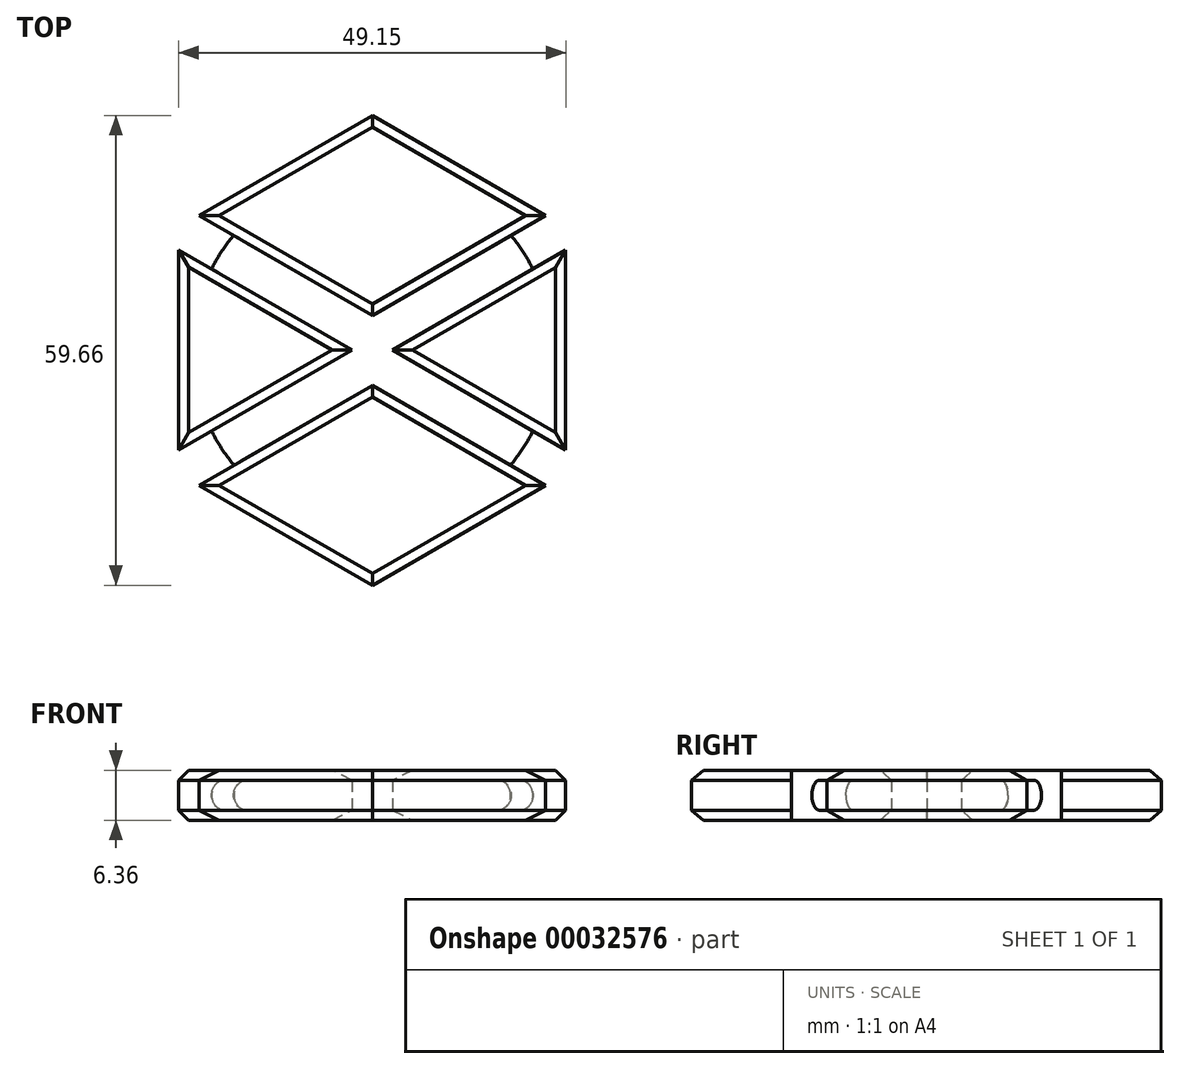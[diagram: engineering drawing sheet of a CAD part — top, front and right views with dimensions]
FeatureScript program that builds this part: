
annotation { "Feature Type Name" : "Feature", "Feature Type Description" : "" }
export const myFeature = defineFeature(function(context is Context, id is Id, definition is map)
    precondition{}
    {
        {
            var Q0;
            Q0=qCreatedBy(makeId("Top.planeOp"),FACE);
            var sketch = newSketch(context, id + "F0", { "sketchPlane" : qUnion([Q0])});
            skLineSegment(sketch, "E0", {"start": v(0, 0) * mm, "end": v(-22, 12.7) * mm});
            skLineSegment(sketch, "E1", {"start": v(-22, 12.7) * mm, "end": v(0, 25.4) * mm});
            skLineSegment(sketch, "E2", {"start": v(0, 25.4) * mm, "end": v(22, 12.7) * mm});
            skLineSegment(sketch, "E3", {"start": v(22, 12.7) * mm, "end": v(0, 0) * mm});
            skLineSegment(sketch, "E4", {"start": v(-2.6, 29.9) * mm, "end": v(-24.6, 17.2) * mm});
            skLineSegment(sketch, "E5", {"start": v(-24.6, 17.2) * mm, "end": v(-24.6, 42.6) * mm});
            skLineSegment(sketch, "E6", {"start": v(-24.6, 42.6) * mm, "end": v(-2.6, 29.9) * mm});
            skLineSegment(sketch, "E7", {"start": v(0, 34.26) * mm, "end": v(-22, 46.96) * mm});
            skLineSegment(sketch, "E8", {"start": v(-22, 46.96) * mm, "end": v(0, 59.66) * mm});
            skLineSegment(sketch, "E9", {"start": v(0, 59.66) * mm, "end": v(22, 46.96) * mm});
            skLineSegment(sketch, "E10", {"start": v(22, 46.96) * mm, "end": v(0, 34.26) * mm});
            skLineSegment(sketch, "E11", {"start": v(2.56, 29.87) * mm, "end": v(24.56, 17.17) * mm});
            skLineSegment(sketch, "E12", {"start": v(24.56, 17.17) * mm, "end": v(24.56, 42.57) * mm});
            skLineSegment(sketch, "E13", {"start": v(24.56, 42.57) * mm, "end": v(2.56, 29.87) * mm});
            skLineSegment(sketch, "E14", {"start": v(0, 25.4) * mm, "end": v(-2.6, 29.9) * mm});
            skLineSegment(sketch, "E15", {"start": v(-2.6, 29.9) * mm, "end": v(0, 34.26) * mm});
            skLineSegment(sketch, "E16", {"start": v(0, 34.26) * mm, "end": v(2.56, 29.87) * mm});
            skLineSegment(sketch, "E17", {"start": v(2.56, 29.87) * mm, "end": v(0, 25.4) * mm});
            skCircle(sketch, "E18", {"center": v(-0.02, 29.89) * mm, "radius": 22.86 * mm});
            skPoint(sketch, "E19", {"position": v(0, 46.96) * mm});
            skSolve(sketch);
        }
        {
            var Q0;
            {var subQ6=sQuery(id+"F0.wireOp",EDGE,"E8");Q0=makeQuery(id+"F0.imprint","IMPRINT",FACE,{"disambiguationData":[TD([[makeQuery(id+"F0.imprint","IMPRINT",EDGE,{"derivedFrom":subQ6}),-1.0]])]});}
            var Q1;
            {var subQ1=sQuery(id+"F0.wireOp",EDGE,"E18");var subQ3=sQuery(id+"F0.wireOp",EDGE,"E7");var subQ5=makeQuery(id+"F0.imprint","INTERSECT",VERTEX,{"derivedFrom":[subQ3,subQ1]});Q1=makeQuery(id+"F0.imprint","IMPRINT",FACE,{"disambiguationData":[TD([[makeQuery(id+"F0.imprint","IMPRINT",EDGE,{"disambiguationData":[TD([[subQ5,1.0]])],"derivedFrom":subQ1}),1.0]])]});}
            var Q2;
            {var subQ0=sQuery(id+"F0.wireOp",EDGE,"E18");var subQ3=sQuery(id+"F0.wireOp",EDGE,"E11");var subQ4=makeQuery(id+"F0.imprint","INTERSECT",VERTEX,{"derivedFrom":[subQ3,subQ0]});Q2=makeQuery(id+"F0.imprint","IMPRINT",FACE,{"disambiguationData":[TD([[makeQuery(id+"F0.imprint","IMPRINT",EDGE,{"disambiguationData":[TD([[subQ4,-1.0]])],"derivedFrom":subQ0}),1.0]])]});}
            var Q3;
            {var subQ5=sQuery(id+"F0.wireOp",EDGE,"E12");Q3=makeQuery(id+"F0.imprint","IMPRINT",FACE,{"disambiguationData":[TD([[makeQuery(id+"F0.imprint","IMPRINT",EDGE,{"derivedFrom":subQ5}),1.0]])]});}
            var Q4;
            {var subQ6=sQuery(id+"F0.wireOp",EDGE,"E0");Q4=makeQuery(id+"F0.imprint","IMPRINT",FACE,{"disambiguationData":[TD([[makeQuery(id+"F0.imprint","IMPRINT",EDGE,{"derivedFrom":subQ6}),-1.0]])]});}
            var Q5;
            {var subQ0=sQuery(id+"F0.wireOp",EDGE,"E18");var subQ3=sQuery(id+"F0.wireOp",EDGE,"E1");var subQ4=makeQuery(id+"F0.imprint","INTERSECT",VERTEX,{"derivedFrom":[subQ3,subQ0]});Q5=makeQuery(id+"F0.imprint","IMPRINT",FACE,{"disambiguationData":[TD([[makeQuery(id+"F0.imprint","IMPRINT",EDGE,{"disambiguationData":[TD([[subQ4,-1.0]])],"derivedFrom":subQ0}),1.0]])]});}
            var Q6;
            {var subQ5=sQuery(id+"F0.wireOp",EDGE,"E5");Q6=makeQuery(id+"F0.imprint","IMPRINT",FACE,{"disambiguationData":[TD([[makeQuery(id+"F0.imprint","IMPRINT",EDGE,{"derivedFrom":subQ5}),-1.0]])]});}
            var Q7;
            {var subQ0=sQuery(id+"F0.wireOp",EDGE,"E18");var subQ3=sQuery(id+"F0.wireOp",EDGE,"E4");var subQ4=makeQuery(id+"F0.imprint","INTERSECT",VERTEX,{"derivedFrom":[subQ3,subQ0]});Q7=makeQuery(id+"F0.imprint","IMPRINT",FACE,{"disambiguationData":[TD([[makeQuery(id+"F0.imprint","IMPRINT",EDGE,{"disambiguationData":[TD([[subQ4,1.0]])],"derivedFrom":subQ0}),1.0]])]});}
            extrude(context, id + "F1", {"entities" : qUnion([Q0, Q1, Q2, Q3, Q4, Q5, Q6, Q7]), "endBound" : BoundingType.SYMMETRIC, "depth" : 6.35 * mm});
        }
        {
            var Q0;
            {var subQ5=sQuery(id+"F0.wireOp",EDGE,"E16");Q0=makeQuery(id+"F0.imprint","IMPRINT",FACE,{"disambiguationData":[TD([[makeQuery(id+"F0.imprint","IMPRINT",EDGE,{"derivedFrom":subQ5}),1.0]])]});}
            var Q1;
            Q1=makeQuery(id+"F0.imprint","IMPRINT",FACE,{"disambiguationData":[TD([[makeQuery(id+"F0.imprint","IMPRINT",EDGE,{"derivedFrom":sQuery(id+"F0.wireOp",EDGE,"E14")}),-1.0]])]});
            var Q2;
            {var subQ5=sQuery(id+"F0.wireOp",EDGE,"E15");Q2=makeQuery(id+"F0.imprint","IMPRINT",FACE,{"disambiguationData":[TD([[makeQuery(id+"F0.imprint","IMPRINT",EDGE,{"derivedFrom":subQ5}),1.0]])]});}
            var Q3;
            {var subQ5=sQuery(id+"F0.wireOp",EDGE,"E14");Q3=makeQuery(id+"F0.imprint","IMPRINT",FACE,{"disambiguationData":[TD([[makeQuery(id+"F0.imprint","IMPRINT",EDGE,{"derivedFrom":subQ5}),1.0]])]});}
            var Q4;
            {var subQ5=sQuery(id+"F0.wireOp",EDGE,"E17");Q4=makeQuery(id+"F0.imprint","IMPRINT",FACE,{"disambiguationData":[TD([[makeQuery(id+"F0.imprint","IMPRINT",EDGE,{"derivedFrom":subQ5}),1.0]])]});}
            extrude(context, id + "F2", {"entities" : qUnion([Q0, Q1, Q2, Q3, Q4]), "endBound" : BoundingType.SYMMETRIC, "depth" : 3.8 * mm});
        }
        {
            var Q0;
            {var subQ0=sQuery(id+"F0.wireOp",EDGE,"E18");Q0=makeQuery(id+"F2.opExtrude","CAP_EDGE",EDGE,{"disambiguationData":[OSD([subQ0]),TDD([makeQuery(id+"F0.imprint","IMPRINT",EDGE,{"disambiguationData":[TD([[makeQuery(id+"F0.imprint","INTERSECT",VERTEX,{"derivedFrom":[sQuery(id+"F0.wireOp",EDGE,"E6"),subQ0]}),1.0]])],"derivedFrom":subQ0})])],"isStart":false});}
            var Q1;
            {var subQ0=sQuery(id+"F0.wireOp",EDGE,"E18");Q1=makeQuery(id+"F2.opExtrude","CAP_EDGE",EDGE,{"disambiguationData":[OSD([subQ0]),TDD([makeQuery(id+"F0.imprint","IMPRINT",EDGE,{"disambiguationData":[TD([[makeQuery(id+"F0.imprint","INTERSECT",VERTEX,{"derivedFrom":[sQuery(id+"F0.wireOp",EDGE,"E6"),subQ0]}),1.0]])],"derivedFrom":subQ0})])],"isStart":true});}
            var Q2;
            {var subQ0=sQuery(id+"F0.wireOp",EDGE,"E18");Q2=makeQuery(id+"F2.opExtrude","CAP_EDGE",EDGE,{"disambiguationData":[OSD([subQ0]),TDD([makeQuery(id+"F0.imprint","IMPRINT",EDGE,{"disambiguationData":[TD([[makeQuery(id+"F0.imprint","INTERSECT",VERTEX,{"derivedFrom":[sQuery(id+"F0.wireOp",EDGE,"E1"),subQ0]}),1.0]])],"derivedFrom":subQ0})])],"isStart":false});}
            var Q3;
            {var subQ0=sQuery(id+"F0.wireOp",EDGE,"E18");Q3=makeQuery(id+"F2.opExtrude","CAP_EDGE",EDGE,{"disambiguationData":[OSD([subQ0]),TDD([makeQuery(id+"F0.imprint","IMPRINT",EDGE,{"disambiguationData":[TD([[makeQuery(id+"F0.imprint","INTERSECT",VERTEX,{"derivedFrom":[sQuery(id+"F0.wireOp",EDGE,"E1"),subQ0]}),1.0]])],"derivedFrom":subQ0})])],"isStart":true});}
            var Q4;
            {var subQ0=sQuery(id+"F0.wireOp",EDGE,"E18");Q4=makeQuery(id+"F2.opExtrude","CAP_EDGE",EDGE,{"disambiguationData":[OSD([subQ0]),TDD([makeQuery(id+"F0.imprint","IMPRINT",EDGE,{"disambiguationData":[TD([[makeQuery(id+"F0.imprint","INTERSECT",VERTEX,{"derivedFrom":[sQuery(id+"F0.wireOp",EDGE,"E2"),subQ0]}),-1.0]])],"derivedFrom":subQ0})])],"isStart":true});}
            var Q5;
            {var subQ0=sQuery(id+"F0.wireOp",EDGE,"E18");Q5=makeQuery(id+"F2.opExtrude","CAP_EDGE",EDGE,{"disambiguationData":[OSD([subQ0]),TDD([makeQuery(id+"F0.imprint","IMPRINT",EDGE,{"disambiguationData":[TD([[makeQuery(id+"F0.imprint","INTERSECT",VERTEX,{"derivedFrom":[sQuery(id+"F0.wireOp",EDGE,"E2"),subQ0]}),-1.0]])],"derivedFrom":subQ0})])],"isStart":false});}
            var Q6;
            {var subQ0=sQuery(id+"F0.wireOp",EDGE,"E18");Q6=makeQuery(id+"F2.opExtrude","CAP_EDGE",EDGE,{"disambiguationData":[OSD([subQ0]),TDD([makeQuery(id+"F0.imprint","IMPRINT",EDGE,{"disambiguationData":[TD([[makeQuery(id+"F0.imprint","INTERSECT",VERTEX,{"derivedFrom":[sQuery(id+"F0.wireOp",EDGE,"E10"),subQ0]}),1.0]])],"derivedFrom":subQ0})])],"isStart":true});}
            var Q7;
            {var subQ0=sQuery(id+"F0.wireOp",EDGE,"E18");Q7=makeQuery(id+"F2.opExtrude","CAP_EDGE",EDGE,{"disambiguationData":[OSD([subQ0]),TDD([makeQuery(id+"F0.imprint","IMPRINT",EDGE,{"disambiguationData":[TD([[makeQuery(id+"F0.imprint","INTERSECT",VERTEX,{"derivedFrom":[sQuery(id+"F0.wireOp",EDGE,"E10"),subQ0]}),1.0]])],"derivedFrom":subQ0})])],"isStart":false});}
            fillet(context, id + "F3", {"entities" : qUnion([Q0, Q1, Q2, Q3, Q4, Q5, Q6, Q7]), "radius" : 1.9 * mm, "tangentPropagation" : true, "allowEdgeOverflow" : false});
        }
        {
            var Q0;
            Q0=makeQuery(id+"F1.opExtrude","CAP_EDGE",EDGE,{"disambiguationData":[OSD([sQuery(id+"F0.wireOp",EDGE,"E8")])],"isStart":false});
            var Q1;
            Q1=makeQuery(id+"F1.opExtrude","CAP_EDGE",EDGE,{"disambiguationData":[OSD([sQuery(id+"F0.wireOp",EDGE,"E8")])],"isStart":true});
            var Q2;
            Q2=makeQuery(id+"F1.opExtrude","CAP_EDGE",EDGE,{"disambiguationData":[OSD([sQuery(id+"F0.wireOp",EDGE,"E9")])],"isStart":true});
            var Q3;
            Q3=makeQuery(id+"F1.opExtrude","CAP_EDGE",EDGE,{"disambiguationData":[OSD([sQuery(id+"F0.wireOp",EDGE,"E9")])],"isStart":false});
            var Q4;
            Q4=makeQuery(id+"F1.opExtrude","CAP_EDGE",EDGE,{"disambiguationData":[OSD([sQuery(id+"F0.wireOp",EDGE,"E12")])],"isStart":false});
            var Q5;
            Q5=makeQuery(id+"F1.opExtrude","CAP_EDGE",EDGE,{"disambiguationData":[OSD([sQuery(id+"F0.wireOp",EDGE,"E12")])],"isStart":true});
            var Q6;
            Q6=makeQuery(id+"F1.opExtrude","CAP_EDGE",EDGE,{"disambiguationData":[OSD([sQuery(id+"F0.wireOp",EDGE,"E0")])],"isStart":true});
            var Q7;
            Q7=makeQuery(id+"F1.opExtrude","CAP_EDGE",EDGE,{"disambiguationData":[OSD([sQuery(id+"F0.wireOp",EDGE,"E0")])],"isStart":false});
            var Q8;
            Q8=makeQuery(id+"F1.opExtrude","CAP_EDGE",EDGE,{"disambiguationData":[OSD([sQuery(id+"F0.wireOp",EDGE,"E3")])],"isStart":false});
            var Q9;
            Q9=makeQuery(id+"F1.opExtrude","CAP_EDGE",EDGE,{"disambiguationData":[OSD([sQuery(id+"F0.wireOp",EDGE,"E3")])],"isStart":true});
            var Q10;
            Q10=makeQuery(id+"F1.opExtrude","CAP_EDGE",EDGE,{"disambiguationData":[OSD([sQuery(id+"F0.wireOp",EDGE,"E5")])],"isStart":true});
            var Q11;
            Q11=makeQuery(id+"F1.opExtrude","CAP_EDGE",EDGE,{"disambiguationData":[OSD([sQuery(id+"F0.wireOp",EDGE,"E5")])],"isStart":false});
            chamfer(context, id + "F4", {"entities" : qUnion([Q0, Q1, Q2, Q3, Q4, Q5, Q6, Q7, Q8, Q9, Q10, Q11]), "width" : 1.27 * mm, "tangentPropagation" : true});
        }
        {
            var Q0;
            Q0=makeQuery(id+"F1.opExtrude","CAP_EDGE",EDGE,{"disambiguationData":[OSD([sQuery(id+"F0.wireOp",EDGE,"E7")])],"isStart":false});
            var Q1;
            Q1=makeQuery(id+"F1.opExtrude","CAP_EDGE",EDGE,{"disambiguationData":[OSD([sQuery(id+"F0.wireOp",EDGE,"E10")])],"isStart":false});
            var Q2;
            Q2=makeQuery(id+"F1.opExtrude","CAP_EDGE",EDGE,{"disambiguationData":[OSD([sQuery(id+"F0.wireOp",EDGE,"E6")])],"isStart":false});
            var Q3;
            Q3=makeQuery(id+"F1.opExtrude","CAP_EDGE",EDGE,{"disambiguationData":[OSD([sQuery(id+"F0.wireOp",EDGE,"E4")])],"isStart":false});
            var Q4;
            Q4=makeQuery(id+"F1.opExtrude","CAP_EDGE",EDGE,{"disambiguationData":[OSD([sQuery(id+"F0.wireOp",EDGE,"E11")])],"isStart":false});
            var Q5;
            Q5=makeQuery(id+"F1.opExtrude","CAP_EDGE",EDGE,{"disambiguationData":[OSD([sQuery(id+"F0.wireOp",EDGE,"E2")])],"isStart":false});
            var Q6;
            Q6=makeQuery(id+"F1.opExtrude","CAP_EDGE",EDGE,{"disambiguationData":[OSD([sQuery(id+"F0.wireOp",EDGE,"E1")])],"isStart":false});
            var Q7;
            Q7=makeQuery(id+"F1.opExtrude","CAP_EDGE",EDGE,{"disambiguationData":[OSD([sQuery(id+"F0.wireOp",EDGE,"E13")])],"isStart":false});
            var Q8;
            Q8=makeQuery(id+"F1.opExtrude","CAP_EDGE",EDGE,{"disambiguationData":[OSD([sQuery(id+"F0.wireOp",EDGE,"E7")])],"isStart":true});
            var Q9;
            Q9=makeQuery(id+"F1.opExtrude","CAP_EDGE",EDGE,{"disambiguationData":[OSD([sQuery(id+"F0.wireOp",EDGE,"E10")])],"isStart":true});
            var Q10;
            Q10=makeQuery(id+"F1.opExtrude","CAP_EDGE",EDGE,{"disambiguationData":[OSD([sQuery(id+"F0.wireOp",EDGE,"E4")])],"isStart":true});
            var Q11;
            Q11=makeQuery(id+"F1.opExtrude","CAP_EDGE",EDGE,{"disambiguationData":[OSD([sQuery(id+"F0.wireOp",EDGE,"E6")])],"isStart":true});
            var Q12;
            Q12=makeQuery(id+"F1.opExtrude","CAP_EDGE",EDGE,{"disambiguationData":[OSD([sQuery(id+"F0.wireOp",EDGE,"E11")])],"isStart":true});
            var Q13;
            Q13=makeQuery(id+"F1.opExtrude","CAP_EDGE",EDGE,{"disambiguationData":[OSD([sQuery(id+"F0.wireOp",EDGE,"E13")])],"isStart":true});
            var Q14;
            Q14=makeQuery(id+"F1.opExtrude","CAP_EDGE",EDGE,{"disambiguationData":[OSD([sQuery(id+"F0.wireOp",EDGE,"E2")])],"isStart":true});
            var Q15;
            Q15=makeQuery(id+"F1.opExtrude","CAP_EDGE",EDGE,{"disambiguationData":[OSD([sQuery(id+"F0.wireOp",EDGE,"E1")])],"isStart":true});
            chamfer(context, id + "F5", {"entities" : qUnion([Q0, Q1, Q2, Q3, Q4, Q5, Q6, Q7, Q8, Q9, Q10, Q11, Q12, Q13, Q14, Q15]), "width" : 1.27 * mm, "tangentPropagation" : true});
        }
    });
